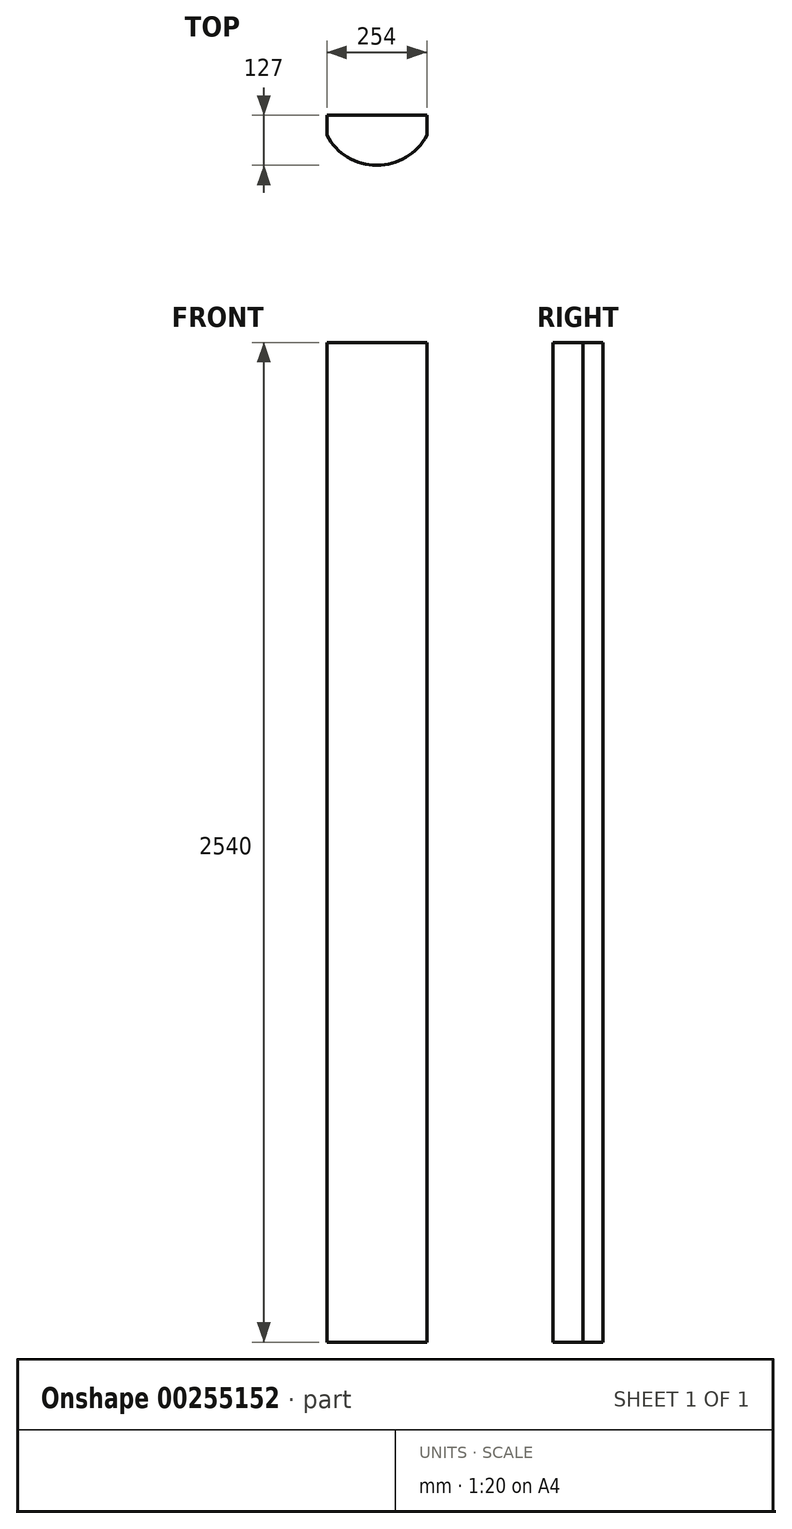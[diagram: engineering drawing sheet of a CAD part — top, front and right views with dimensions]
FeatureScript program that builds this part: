
annotation { "Feature Type Name" : "Feature", "Feature Type Description" : "" }
export const myFeature = defineFeature(function(context is Context, id is Id, definition is map)
    precondition{}
    {
        {
            var Q0;
            Q0=qCreatedBy(makeId("Top.planeOp"),FACE);
            var sketch = newSketch(context, id + "F0", { "sketchPlane" : qUnion([Q0])});
            skLineSegment(sketch, "E0", {"start": v(0, 0) * mm, "end": v(254, 0) * mm});
            skPoint(sketch, "E1", {"position": v(127, 0) * mm});
            skLineSegment(sketch, "E2", {"start": v(0, 0) * mm, "end": v(0, -50.8) * mm});
            skLineSegment(sketch, "E3", {"start": v(254, 0) * mm, "end": v(254, -50.8) * mm});
            skArc(sketch, "E4", {"start": v(0, -50.8) * mm, "mid": v(127, -127) * mm, "end": v(254, -50.8) * mm});
            skPoint(sketch, "E5.end.orphan", {"position": v(127, -127) * mm});
            skSolve(sketch);
        }
        {
            var Q0;
            Q0=makeQuery(id+"F0.imprint","IMPRINT",FACE,{"disambiguationData":[TD([[makeQuery(id+"F0.imprint","IMPRINT",EDGE,{"derivedFrom":sQuery(id+"F0.wireOp",EDGE,"E0")}),-1.0]])]});
            extrude(context, id + "F1", {"entities" : qUnion([Q0]), "depth" : 2540 * mm});
        }
    });
